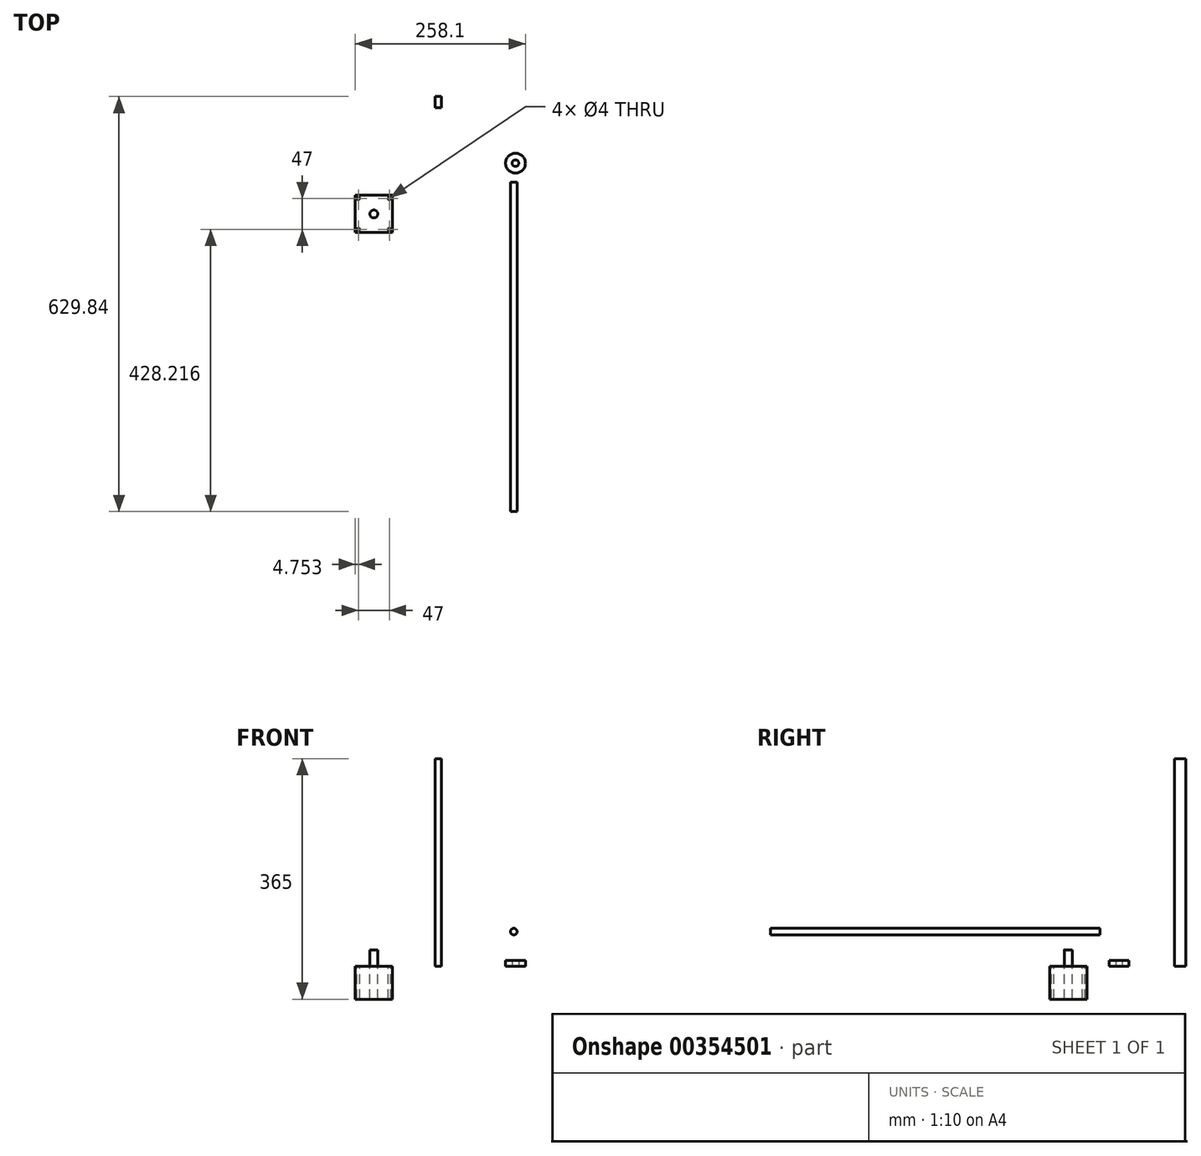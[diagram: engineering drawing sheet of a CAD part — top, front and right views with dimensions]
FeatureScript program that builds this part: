
annotation { "Feature Type Name" : "Feature", "Feature Type Description" : "" }
export const myFeature = defineFeature(function(context is Context, id is Id, definition is map)
    precondition{}
    {
        {
            var Q0;
            Q0=qCreatedBy(makeId("Top.planeOp"),FACE);
            var sketch = newSketch(context, id + "F0", { "sketchPlane" : qUnion([Q0])});
            skLineSegment(sketch, "E0.bottom", {"start": v(-141.4, -76.53) * mm, "end": v(-84.9, -76.53) * mm});
            skLineSegment(sketch, "E0.top", {"start": v(-141.4, -20.03) * mm, "end": v(-84.9, -20.03) * mm});
            skLineSegment(sketch, "E0.left", {"start": v(-141.4, -76.53) * mm, "end": v(-141.4, -20.03) * mm});
            skLineSegment(sketch, "E0.right", {"start": v(-84.9, -76.53) * mm, "end": v(-84.9, -20.03) * mm});
            skCircle(sketch, "E1", {"center": v(-113.16, -48.28) * mm, "radius": 6 * mm});
            skCircle(sketch, "E2", {"center": v(-136.66, -24.78) * mm, "radius": 2 * mm});
            skCircle(sketch, "E3", {"center": v(-89.66, -24.78) * mm, "radius": 2 * mm});
            skCircle(sketch, "E4", {"center": v(-89.66, -71.78) * mm, "radius": 2 * mm});
            skCircle(sketch, "E5", {"center": v(-136.66, -71.78) * mm, "radius": 2 * mm});
            skSolve(sketch);
        }
        {
            var Q0;
            Q0=makeQuery(id+"F0.imprint","IMPRINT",FACE,{"disambiguationData":[TD([[makeQuery(id+"F0.imprint","IMPRINT",EDGE,{"derivedFrom":sQuery(id+"F0.wireOp",EDGE,"E1")}),1.0]])]});
            extrude(context, id + "F1", {"entities" : qUnion([Q0]), "depth" : 25 * mm});
        }
        {
            var Q0;
            Q0 = qSketchRegion(id + "F0", true);
            extrude(context, id + "F2", {"entities" : qUnion([Q0]), "oppositeDirection" : true, "depth" : 50 * mm});
        }
        {
            var Q0;
            Q0=qCreatedBy(makeId("Top.planeOp"),FACE);
            var sketch = newSketch(context, id + "F3", { "sketchPlane" : qUnion([Q0])});
            skCircle(sketch, "E6", {"center": v(101.7, 28.74) * mm, "radius": 15 * mm});
            skCircle(sketch, "E7", {"center": v(101.7, 28.74) * mm, "radius": 5 * mm});
            skSolve(sketch);
        }
        {
            var Q0;
            Q0=makeQuery(id+"F3.imprint","IMPRINT",FACE,{"disambiguationData":[TD([[makeQuery(id+"F3.imprint","IMPRINT",EDGE,{"derivedFrom":sQuery(id+"F3.wireOp",EDGE,"E6")}),1.0]])]});
            extrude(context, id + "F4", {"entities" : qUnion([Q0]), "depth" : 9 * mm});
        }
        {
            var Q0;
            Q0=qCreatedBy(makeId("Front.planeOp"),FACE);
            var sketch = newSketch(context, id + "F5", { "sketchPlane" : qUnion([Q0])});
            skCircle(sketch, "E8", {"center": v(99.12, 52.52) * mm, "radius": 5 * mm});
            skSolve(sketch);
        }
        {
            var Q0;
            Q0 = qSketchRegion(id + "F5", true);
            extrude(context, id + "F6", {"entities" : qUnion([Q0]), "depth" : 500 * mm});
        }
        {
            var Q0;
            Q0=qCreatedBy(makeId("Top.planeOp"),FACE);
            var sketch = newSketch(context, id + "F7", { "sketchPlane" : qUnion([Q0])});
            skLineSegment(sketch, "E9.bottom", {"start": v(-10.68, 112.84) * mm, "end": v(-20.18, 112.84) * mm});
            skLineSegment(sketch, "E9.top", {"start": v(-10.68, 129.84) * mm, "end": v(-20.18, 129.84) * mm});
            skLineSegment(sketch, "E9.left", {"start": v(-10.68, 112.84) * mm, "end": v(-10.68, 129.84) * mm});
            skLineSegment(sketch, "E9.right", {"start": v(-20.18, 112.84) * mm, "end": v(-20.18, 129.84) * mm});
            skPoint(sketch, "E9.middle", {"position": v(-15.43, 121.34) * mm});
            skSolve(sketch);
        }
        {
            var Q0;
            Q0 = qSketchRegion(id + "F7", true);
            extrude(context, id + "F8", {"entities" : qUnion([Q0]), "depth" : 315 * mm});
        }
    });
